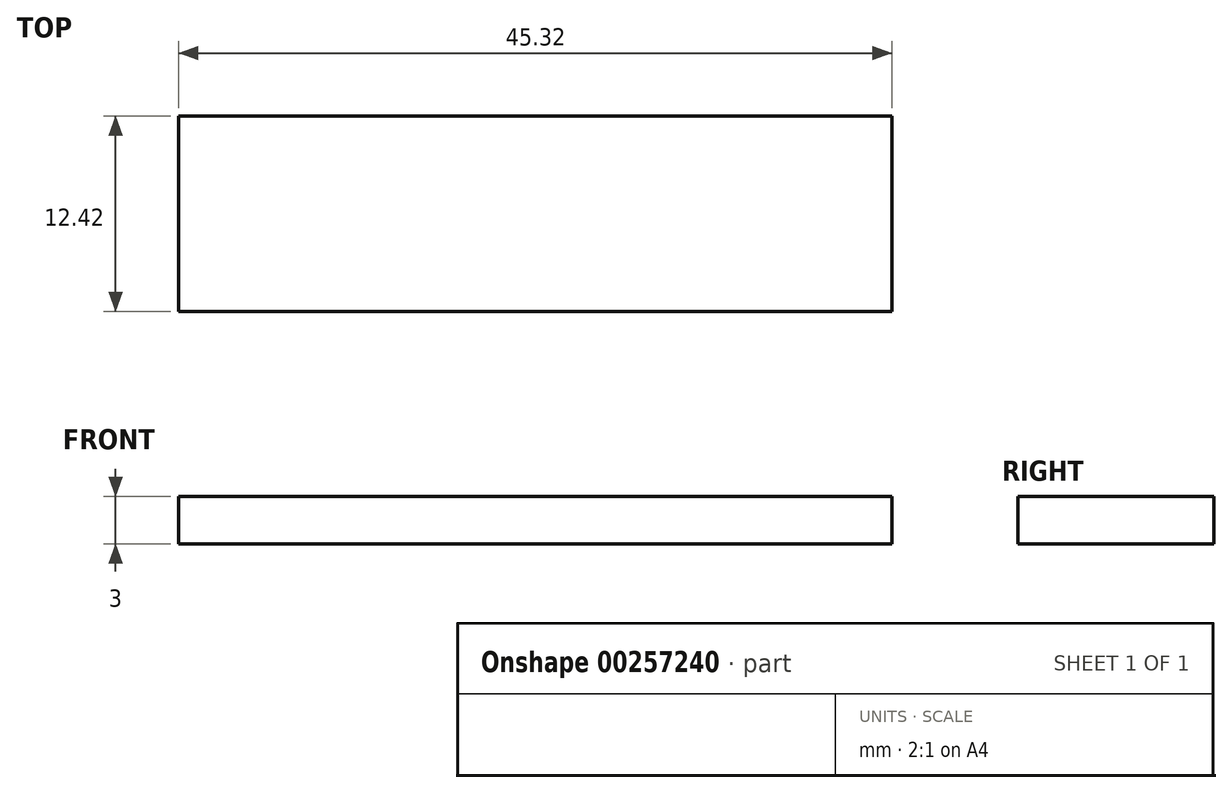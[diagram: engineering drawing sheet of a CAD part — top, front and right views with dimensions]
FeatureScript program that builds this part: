
annotation { "Feature Type Name" : "Feature", "Feature Type Description" : "" }
export const myFeature = defineFeature(function(context is Context, id is Id, definition is map)
    precondition{}
    {
        {
            var Q0;
            Q0=qCreatedBy(makeId("Top.planeOp"),FACE);
            var sketch = newSketch(context, id + "F0", { "sketchPlane" : qUnion([Q0])});
            skLineSegment(sketch, "E0.bottom", {"start": v(22.66, -6.21) * mm, "end": v(-22.66, -6.21) * mm});
            skLineSegment(sketch, "E0.top", {"start": v(22.66, 6.21) * mm, "end": v(-22.66, 6.21) * mm});
            skLineSegment(sketch, "E0.left", {"start": v(22.66, -6.21) * mm, "end": v(22.66, 6.21) * mm});
            skLineSegment(sketch, "E0.right", {"start": v(-22.66, -6.21) * mm, "end": v(-22.66, 6.21) * mm});
            skPoint(sketch, "E0.middle", {"position": v(0, 0) * mm});
            skSolve(sketch);
        }
        {
            var Q0;
            Q0=makeQuery(id+"F0.imprint","IMPRINT",FACE,{"disambiguationData":[TD([[makeQuery(id+"F0.imprint","IMPRINT",EDGE,{"derivedFrom":sQuery(id+"F0.wireOp",EDGE,"E0.bottom")}),-1.0]])]});
            extrude(context, id + "F1", {"entities" : qUnion([Q0]), "oppositeDirection" : true, "depth" : 3 * mm});
        }
    });
